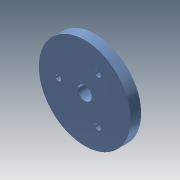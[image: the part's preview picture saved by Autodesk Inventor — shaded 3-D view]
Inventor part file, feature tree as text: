
AUTODESK INVENTOR PART (.ipt)
format: ipt  version: 2013 (Build 170138000, 138)  size: 105,984 bytes
history: native  units: mm
features: extrude x3, sketch x3
ambient origin geometry x8: Origin, YZ Plane, XZ Plane, XY Plane, X Axis, Y Axis, Z Axis, Center Point
bodies: Solid1 (feature_tree)
feature tree (6):
  extrude  "Extrusion1"  Depth=5.0mm
  extrude  "Extrusion2"  Depth=3.0mm
  extrude  "Extrusion3"  Depth=3.0mm
  sketch  "Sketch1"  dims[d0=33.15mm d1=5.0mm]
  sketch  "Sketch2"  dims[d2=3.8mm d3=0.0mm d4=3.0mm]
  sketch  "Sketch3"  dims[d7=3.0mm d8=3.0mm d9=3.8mm d10=0.0mm d11=2.0mm d12=2.0mm d13=2.0mm d14=3.8mm d15=0.0mm]
